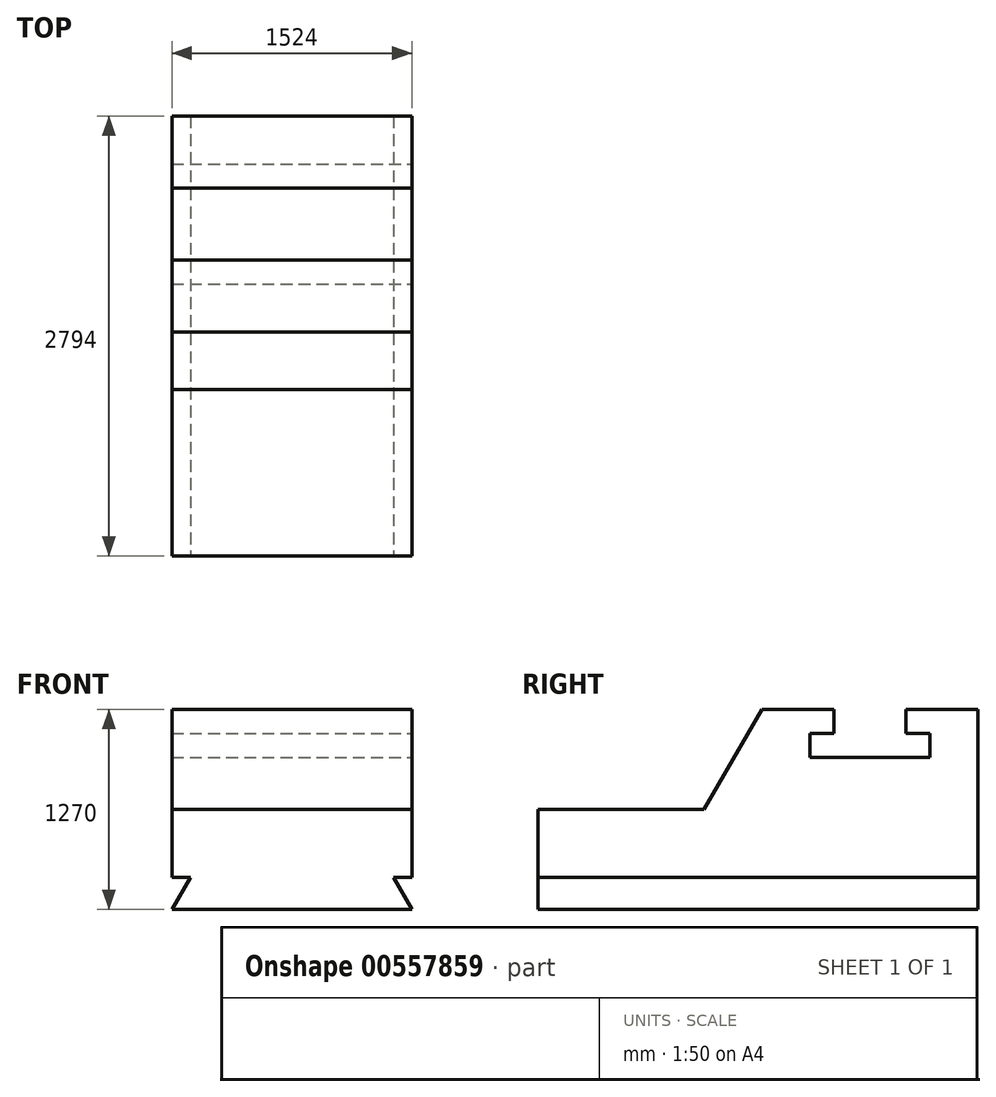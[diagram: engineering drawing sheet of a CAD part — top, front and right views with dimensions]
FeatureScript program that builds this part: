
annotation { "Feature Type Name" : "Feature", "Feature Type Description" : "" }
export const myFeature = defineFeature(function(context is Context, id is Id, definition is map)
    precondition{}
    {
        {
            var Q0;
            Q0=qCreatedBy(makeId("Right.planeOp"),FACE);
            var sketch = newSketch(context, id + "F0", { "sketchPlane" : qUnion([Q0])});
            skLineSegment(sketch, "E0", {"start": v(-70.02, -79.09) * mm, "end": v(-70.02, 352.71) * mm});
            skLineSegment(sketch, "E1", {"start": v(-70.02, -79.09) * mm, "end": v(2723.98, -79.09) * mm});
            skLineSegment(sketch, "E2", {"start": v(2723.98, -79.09) * mm, "end": v(2723.98, 987.71) * mm});
            skLineSegment(sketch, "E3", {"start": v(2723.98, 987.71) * mm, "end": v(2266.78, 987.71) * mm});
            skLineSegment(sketch, "E4", {"start": v(2266.78, 987.71) * mm, "end": v(2266.78, 835.31) * mm});
            skLineSegment(sketch, "E5", {"start": v(2266.78, 835.31) * mm, "end": v(2419.18, 835.31) * mm});
            skLineSegment(sketch, "E6", {"start": v(2419.18, 835.31) * mm, "end": v(2419.18, 682.91) * mm});
            skLineSegment(sketch, "E7", {"start": v(2419.18, 682.91) * mm, "end": v(1657.18, 682.91) * mm});
            skLineSegment(sketch, "E8", {"start": v(1657.18, 682.91) * mm, "end": v(1657.18, 835.31) * mm});
            skLineSegment(sketch, "E9", {"start": v(1657.18, 835.31) * mm, "end": v(1809.58, 835.31) * mm});
            skLineSegment(sketch, "E10", {"start": v(1809.58, 835.31) * mm, "end": v(1809.58, 987.71) * mm});
            skLineSegment(sketch, "E11", {"start": v(1809.58, 987.71) * mm, "end": v(1352.38, 987.71) * mm});
            skLineSegment(sketch, "E12", {"start": v(-70.02, 352.71) * mm, "end": v(985.76, 352.71) * mm});
            skLineSegment(sketch, "E13", {"start": v(1352.38, 987.71) * mm, "end": v(985.76, 352.71) * mm});
            skSolve(sketch);
        }
        {
            var Q0;
            Q0=makeQuery(id+"F0.imprint","IMPRINT",FACE,{"disambiguationData":[TD([[makeQuery(id+"F0.imprint","IMPRINT",EDGE,{"derivedFrom":sQuery(id+"F0.wireOp",EDGE,"E0")}),-1.0]])]});
            extrude(context, id + "F1", {"entities" : qUnion([Q0]), "oppositeDirection" : true, "depth" : 1524 * mm, "offsetDistance" : 25.4 * mm});
        }
        {
            var Q0;
            Q0=makeQuery(id+"F1.opExtrude","SWEPT_FACE",FACE,{"disambiguationData":[OSD([sQuery(id+"F0.wireOp",EDGE,"E0")])]});
            var sketch = newSketch(context, id + "F2", { "sketchPlane" : qUnion([Q0])});
            skLineSegment(sketch, "E14", {"start": v(-1524, -282.29) * mm, "end": v(0, -282.29) * mm});
            skLineSegment(sketch, "E15", {"start": v(-1524, -282.29) * mm, "end": v(-1406.68, -79.09) * mm});
            skLineSegment(sketch, "E16", {"start": v(0, -282.29) * mm, "end": v(-117.32, -79.09) * mm});
            skSolve(sketch);
        }
        {
            var Q0;
            Q0=makeQuery(id+"F2.imprint","IMPRINT",FACE,{"disambiguationData":[TD([[makeQuery(id+"F2.imprint","IMPRINT",EDGE,{"derivedFrom":sQuery(id+"F2.wireOp",EDGE,"E14")}),1.0]])]});
            extrude(context, id + "F3", {"entities" : qUnion([Q0]), "operationType" : NewBodyOperationType.ADD, "oppositeDirection" : true, "depth" : 2794 * mm, "offsetDistance" : 25.4 * mm});
        }
    });
